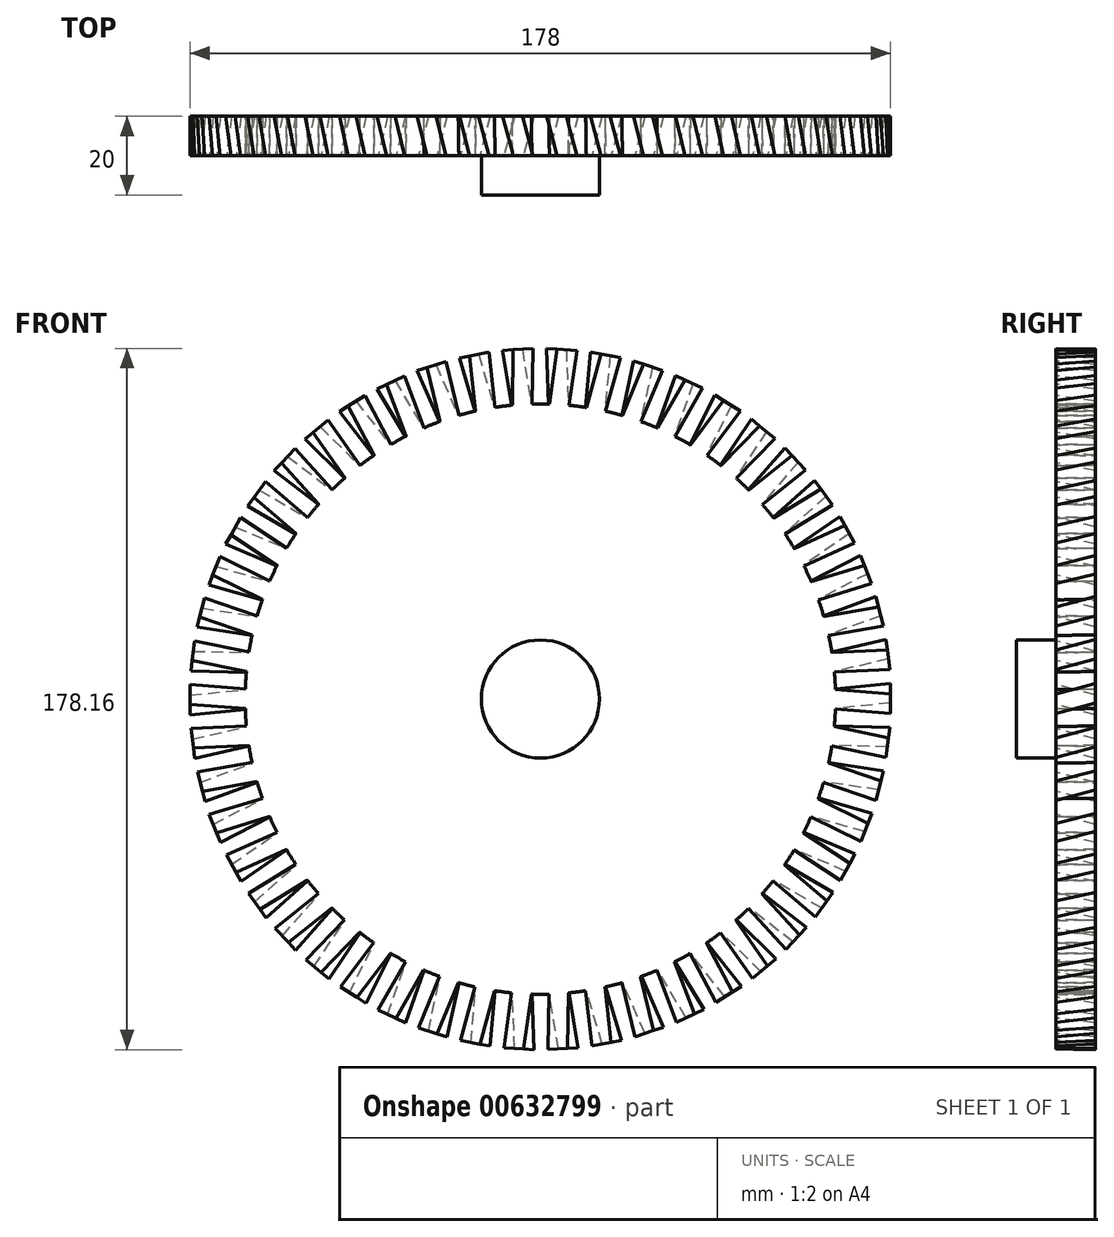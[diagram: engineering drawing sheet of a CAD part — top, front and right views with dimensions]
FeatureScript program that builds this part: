
annotation { "Feature Type Name" : "Feature", "Feature Type Description" : "" }
export const myFeature = defineFeature(function(context is Context, id is Id, definition is map)
    precondition{}
    {
        {
            var Q0;
            Q0=qCreatedBy(makeId("Front.planeOp"),FACE);
            var sketch = newSketch(context, id + "F0", { "sketchPlane" : qUnion([Q0])});
            skCircle(sketch, "E0", {"center": v(0, 0) * mm, "radius": 75 * mm});
            skSolve(sketch);
        }
        {
            var Q0;
            Q0=makeQuery(id+"F0.imprint","IMPRINT",FACE,{"disambiguationData":[TD([[makeQuery(id+"F0.imprint","IMPRINT",EDGE,{"derivedFrom":sQuery(id+"F0.wireOp",EDGE,"E0")}),1.0]])]});
            extrude(context, id + "F1", {"entities" : qUnion([Q0]), "depth" : 10 * mm, "offsetDistance" : 25 * mm});
        }
        {
            var Q0;
            Q0=qCreatedBy(makeId("Right.planeOp"),FACE);
            cPlane(context, id + "F2", {"entities" : qUnion([Q0]), "cplaneType" : CPlaneType.OFFSET, "offset" : 74 * mm, "width" : 150 * mm, "height" : 150 * mm});
        }
        {
            var Q0;
            Q0=qCreatedBy(id+"F2.planeOp",FACE);
            cPlane(context, id + "F3", {"entities" : qUnion([Q0]), "cplaneType" : CPlaneType.OFFSET, "offset" : 15 * mm, "width" : 150 * mm, "height" : 150 * mm});
        }
        {
            var Q0;
            Q0=qCreatedBy(id+"F2.planeOp",FACE);
            var sketch = newSketch(context, id + "F4", { "sketchPlane" : qUnion([Q0])});
            skLineSegment(sketch, "E1", {"start": v(0, 2.5) * mm, "end": v(-10, 2.5) * mm});
            skLineSegment(sketch, "E2", {"start": v(0, -2.5) * mm, "end": v(-10, -2.5) * mm});
            skLineSegment(sketch, "E3", {"start": v(-10, 2.5) * mm, "end": v(-10, -2.5) * mm});
            skLineSegment(sketch, "E4", {"start": v(0, 2.5) * mm, "end": v(0, -2.5) * mm});
            skSolve(sketch);
        }
        {
            var Q0;
            Q0=qCreatedBy(id+"F3.planeOp",FACE);
            var sketch = newSketch(context, id + "F5", { "sketchPlane" : qUnion([Q0])});
            skLineSegment(sketch, "E5", {"start": v(0, 4) * mm, "end": v(-10, 1.32) * mm});
            skLineSegment(sketch, "E6", {"start": v(0, -1) * mm, "end": v(-10, -3.68) * mm});
            skLineSegment(sketch, "E7", {"start": v(-10, 1.32) * mm, "end": v(-10, -3.68) * mm});
            skLineSegment(sketch, "E8", {"start": v(0, 4) * mm, "end": v(0, -1) * mm});
            skSolve(sketch);
        }
        {
            var Q0;
            Q0=makeQuery(id+"F5.imprint","IMPRINT",FACE,{"disambiguationData":[TD([[makeQuery(id+"F5.imprint","IMPRINT",EDGE,{"derivedFrom":sQuery(id+"F5.wireOp",EDGE,"E5")}),1.0]])]});
            var Q1;
            Q1 = qSketchRegion(id + "F4", true);
            loft(context, id + "F6", {"sheetProfilesArray" : [{ "sheetProfileEntities" : qUnion([Q0]) }, { "sheetProfileEntities" : qUnion([Q1]) }]});
        }
        {
            var Q0;
            Q0=makeQuery(id+"F6.opLoft","SWEPT_BODY",BODY,{"disambiguationData":[OSD([makeQuery(id+"F4.imprint","IMPRINT",FACE,{"disambiguationData":[TD([[makeQuery(id+"F4.imprint","IMPRINT",EDGE,{"derivedFrom":sQuery(id+"F4.wireOp",EDGE,"E1")}),1.0]])]}),makeQuery(id+"F5.imprint","IMPRINT",FACE,{"disambiguationData":[TD([[makeQuery(id+"F5.imprint","IMPRINT",EDGE,{"derivedFrom":sQuery(id+"F5.wireOp",EDGE,"E5")}),1.0]])]})])]});
            var Q1;
            Q1=makeQuery(id+"F1.opExtrude","CAP_EDGE",EDGE,{"disambiguationData":[OSD([sQuery(id+"F0.wireOp",EDGE,"E0")])],"isStart":false});
            circularPattern(context, id + "F7", {"operationType" : NewBodyOperationType.ADD, "entities" : qUnion([Q0]), "axis" : qUnion([Q1]), "angle" : 360 * degree, "instanceCount" : 50, "oppositeDirection" : true, "equalSpace" : true, "isCentered" : true});
        }
        {
            var Q0;
            Q0=makeQuery(id+"F1.opExtrude","CAP_FACE",FACE,{"disambiguationData":[OSD([sQuery(id+"F0.wireOp",EDGE,"E0")])],"isStart":false});
            var sketch = newSketch(context, id + "F8", { "sketchPlane" : qUnion([Q0])});
            skCircle(sketch, "E9", {"center": v(0, 0) * mm, "radius": 15 * mm});
            skSolve(sketch);
        }
        {
            var Q0;
            Q0=makeQuery(id+"F8.imprint","IMPRINT",FACE,{"disambiguationData":[TD([[makeQuery(id+"F8.imprint","IMPRINT",EDGE,{"derivedFrom":sQuery(id+"F8.wireOp",EDGE,"E9")}),1.0]])]});
            extrude(context, id + "F9", {"entities" : qUnion([Q0]), "operationType" : NewBodyOperationType.ADD, "depth" : 10 * mm, "offsetDistance" : 25 * mm});
        }
    });
